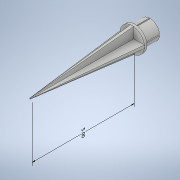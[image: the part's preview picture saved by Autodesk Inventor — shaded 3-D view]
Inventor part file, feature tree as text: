
AUTODESK INVENTOR PART (.ipt)
format: ipt  version: 2021.2 (Build 252289000, 289)  size: 200,192 bytes
history: native  units: in
note: dims shown in document units (in); Inventor stores cm internally (conversion verified against a paired STEP export)
features: sketch x4, extrude x3, other x2, plane x1, loft x1
ambient origin geometry x8: Origin, YZ Plane, XZ Plane, XY Plane, X Axis, Y Axis, Z Axis, Center Point
bodies: Solid1 (feature_tree)
feature tree (11):
  other  "Annotations"
  extrude  "Extrusion1"  Depth=0.125in
  extrude  "Extrusion2"  Depth=0.94in
  sketch  "Sketch4"  dims[d4=0.75in d5=0.0in]
  plane  "Work Plane1"
  loft  "Loft1"
  extrude  "Extrusion3"  Depth=0.05in
  sketch  "Sketch1"  dims[d0=1.2in d1=0.125in]
  sketch  "Sketch2"  dims[d2=0.0in d3=0.94in]
  sketch  "Sketch6"  dims[d7=0.6in d8=0.6in d31=0.15in d10=0.075in d11=0.15in d12=5.0in d14=0.0in d15=90.0deg d16=0.0in d17=90.0deg d18=0.05in d19=1.04in d20=0.65in d21=0.0in d32=0.05in d33=0.0262in d34=0.1634in d35=5.0in]
  other  "Linear Dimension 1"
